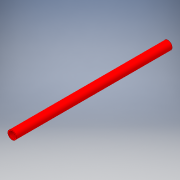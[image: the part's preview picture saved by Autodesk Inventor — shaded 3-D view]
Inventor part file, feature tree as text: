
AUTODESK INVENTOR PART (.ipt)
format: ipt  version: 2018 (Build 220112000, 112)  size: 105,472 bytes
history: native  units: in
note: dims shown in document units (in); Inventor stores cm internally (conversion verified against a paired STEP export)
features: extrude x1, sketch x1
ambient origin geometry x8: Origin, YZ Plane, XZ Plane, XY Plane, X Axis, Y Axis, Z Axis, Center Point
bodies: Solid1 (feature_tree)
feature tree (2):
  extrude  "Extrusion1"  Depth=24.0in
  sketch  "Sketch1"  dims[d0=1.315in d1=1.0in d2=24.0in d3=0.0in]
